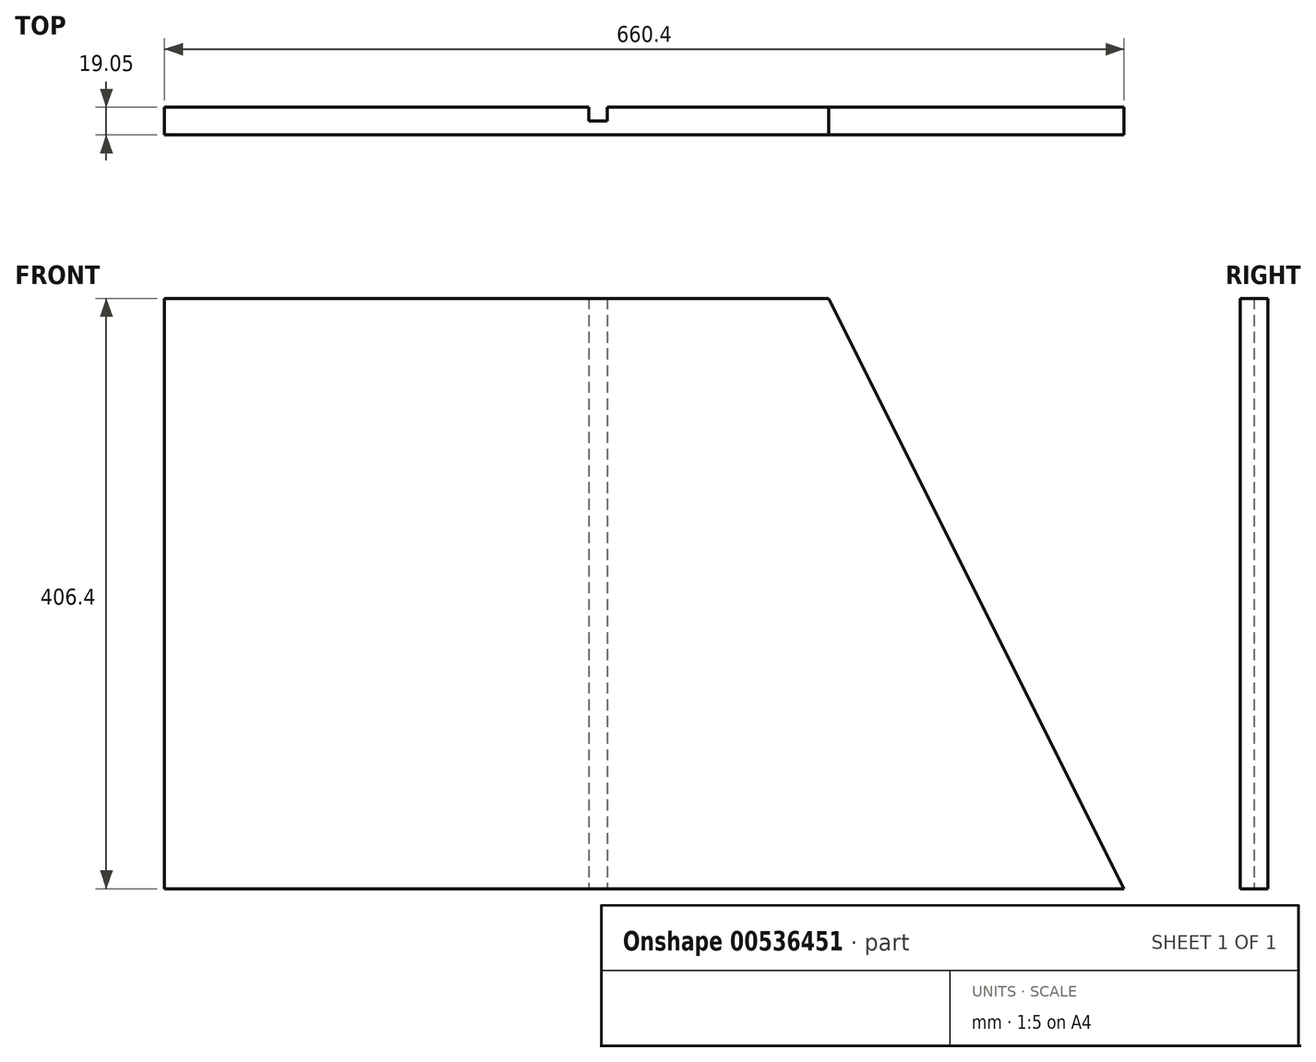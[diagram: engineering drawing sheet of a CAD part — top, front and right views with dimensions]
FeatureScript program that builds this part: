
annotation { "Feature Type Name" : "Feature", "Feature Type Description" : "" }
export const myFeature = defineFeature(function(context is Context, id is Id, definition is map)
    precondition{}
    {
        {
            var Q0;
            Q0=qCreatedBy(makeId("Front.planeOp"),FACE);
            var sketch = newSketch(context, id + "F0", { "sketchPlane" : qUnion([Q0])});
            skLineSegment(sketch, "E0", {"start": v(-356.65, 252.41) * mm, "end": v(-229.65, 252.41) * mm});
            skLineSegment(sketch, "E1", {"start": v(-229.65, 252.41) * mm, "end": v(-26.45, -153.99) * mm});
            skLineSegment(sketch, "E2", {"start": v(-26.45, -153.99) * mm, "end": v(-686.85, -153.99) * mm});
            skLineSegment(sketch, "E3", {"start": v(-229.65, 252.41) * mm, "end": v(-229.65, -153.99) * mm, "construction": true});
            skLineSegment(sketch, "E4.bottom", {"start": v(-356.65, 252.41) * mm, "end": v(-686.85, 252.41) * mm});
            skLineSegment(sketch, "E4.top", {"start": v(-356.65, -153.99) * mm, "end": v(-686.85, -153.99) * mm});
            skLineSegment(sketch, "E4.right", {"start": v(-686.85, 252.41) * mm, "end": v(-686.85, -153.99) * mm});
            skSolve(sketch);
        }
        {
            var Q0;
            {var subQ0=sQuery(id+"F0.wireOp",EDGE,"nFMApCBA-aBbS-xDlN-ZNX0-Un9WT2dHDHLE");Q0=makeQuery(id+"F0.imprint","IMPRINT",FACE,{"disambiguationData":[TD([[makeQuery(id+"F0.imprint","IMPRINT",EDGE,{"derivedFrom":subQ0}),-1.0]])]});}
            var Q1;
            Q1=makeQuery(id+"F0.imprint","IMPRINT",FACE,{"disambiguationData":[TD([[makeQuery(id+"F0.imprint","IMPRINT",EDGE,{"derivedFrom":sQuery(id+"F0.wireOp",EDGE,"E0")}),-1.0]])]});
            var Q2;
            {var subQ0=sQuery(id+"F0.wireOp",EDGE,"E1");Q2=makeQuery(id+"F0.imprint","IMPRINT",FACE,{"disambiguationData":[TD([[makeQuery(id+"F0.imprint","IMPRINT",EDGE,{"derivedFrom":subQ0}),-1.0]])]});}
            extrude(context, id + "F1", {"entities" : qUnion([Q0, Q1, Q2]), "depth" : 19.05 * mm, "offsetDistance" : 25.4 * mm});
        }
        {
            var Q0;
            Q0=makeQuery(id+"F1.opExtrude","CAP_FACE",FACE,{"disambiguationData":[OSD([sQuery(id+"F0.wireOp",EDGE,"E0"),sQuery(id+"F0.wireOp",EDGE,"E1"),sQuery(id+"F0.wireOp",EDGE,"E2"),sQuery(id+"F0.wireOp",EDGE,"nFMApCBA-aBbS-xDlN-ZNX0-Un9WT2dHDHLE")])],"isStart":true});
            var sketch = newSketch(context, id + "F2", { "sketchPlane" : qUnion([Q0])});
            skLineSegment(sketch, "E5", {"start": v(229.65, 252.41) * mm, "end": v(229.65, -153.99) * mm});
            skLineSegment(sketch, "E6.0", {"start": v(382.05, 252.41) * mm, "end": v(382.05, -153.99) * mm});
            skLineSegment(sketch, "E7.0", {"start": v(394.75, 252.41) * mm, "end": v(394.75, -153.99) * mm});
            skLineSegment(sketch, "E8.bottom", {"start": v(394.75, 252.41) * mm, "end": v(382.05, 252.41) * mm});
            skLineSegment(sketch, "E8.top", {"start": v(394.75, -153.99) * mm, "end": v(382.05, -153.99) * mm});
            skSolve(sketch);
        }
        {
            var Q0;
            Q0 = qSketchRegion(id + "F2", true);
            extrude(context, id + "F3", {"entities" : qUnion([Q0]), "operationType" : NewBodyOperationType.REMOVE, "oppositeDirection" : true, "depth" : 9.52 * mm, "offsetDistance" : 25.4 * mm});
        }
    });
